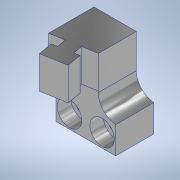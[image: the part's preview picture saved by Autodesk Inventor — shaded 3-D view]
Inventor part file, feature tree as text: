
AUTODESK INVENTOR PART (.ipt)
format: ipt  version: 2022 (Build 260153000, 153)  size: 167,424 bytes
history: native  units: mm
features: sketch x4, other x3, extrude x3, fillet x1
ambient origin geometry x8: Origin, YZ Plane, XZ Plane, XY Plane, X Axis, Y Axis, Z Axis, Center Point
bodies: Solid1 (feature_tree)
feature tree (11):
  other  "Mono_10deg.iam"
  other  "Anschluss_Finger_10deg.ipt:1"
  other  "Anschluss_Greifer.ipt:1"
  fillet  "Fillet1"  Radius=10.0mm
  extrude  "Extrusion1"  Depth=7.0mm TaperAngle=0.0deg
  extrude  "Extrusion2"  Depth=9.0mm
  extrude  "Extrusion3"  Depth=5.0mm TaperAngle=0.0deg
  sketch  "Sketch4"  dims[d6=5.0mm d7=0.0mm d8=17.0mm d9=0.0mm]
  sketch  "Sketch2"  dims[d1=7.0mm d2=4.0mm d3=0.0mm]
  sketch  "Sketch3"  dims[d4=9.0mm d5=9.0mm]
  sketch  "Sketch5"  dims[d10=0.5mm d11=0.872665mm]
